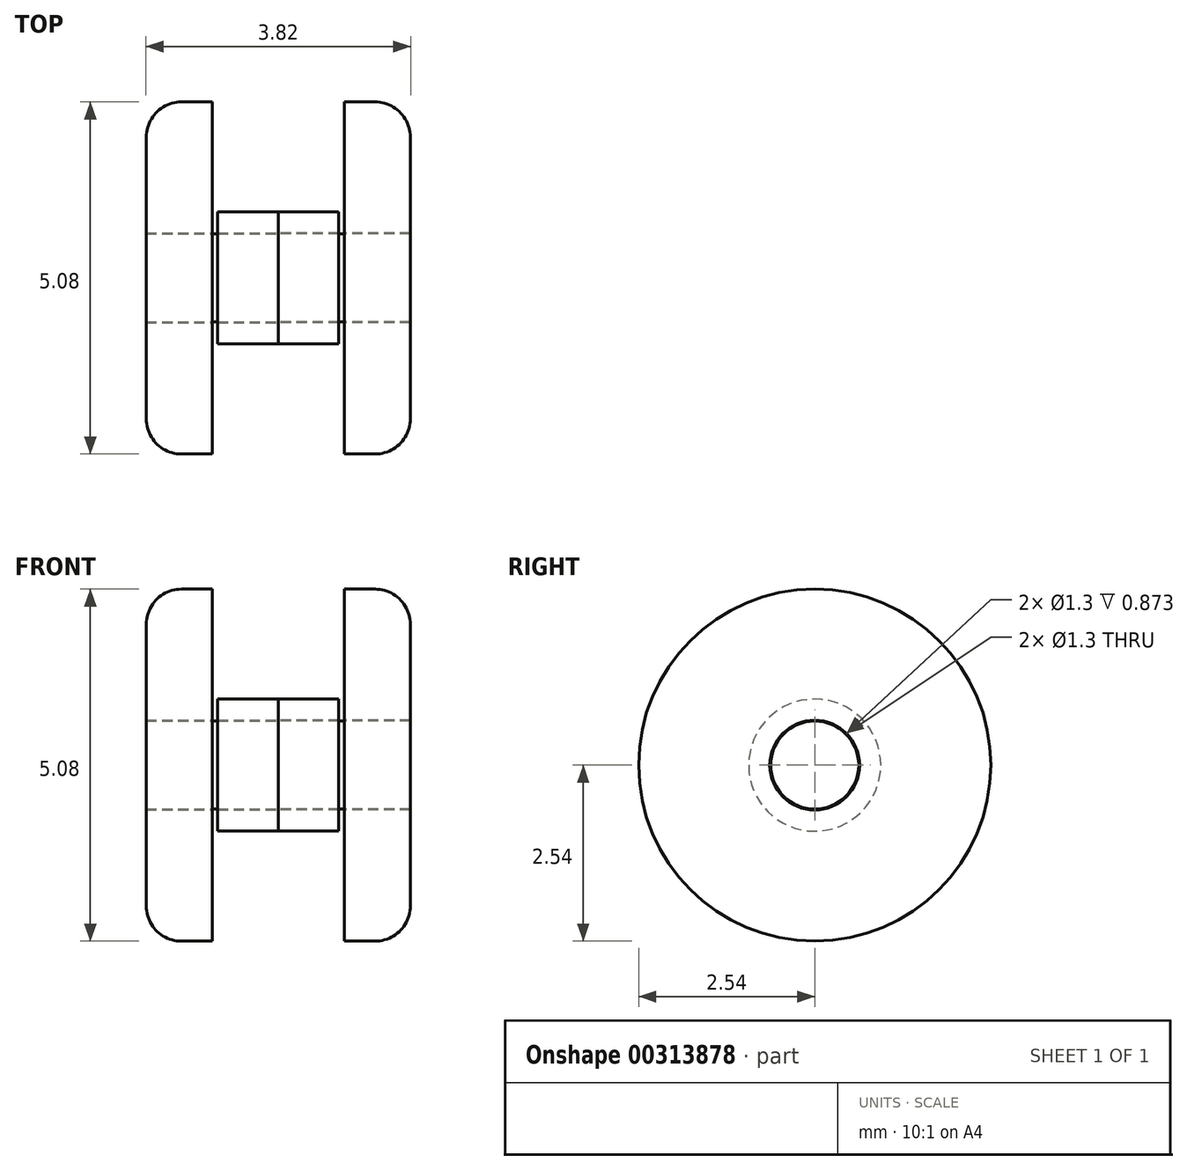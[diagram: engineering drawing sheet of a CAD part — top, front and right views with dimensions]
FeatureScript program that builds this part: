
annotation { "Feature Type Name" : "Feature", "Feature Type Description" : "" }
export const myFeature = defineFeature(function(context is Context, id is Id, definition is map)
    precondition{}
    {
        {
            var Q0;
            Q0=qCreatedBy(makeId("Right.planeOp"),FACE);
            var sketch = newSketch(context, id + "F0", { "sketchPlane" : qUnion([Q0])});
            skCircle(sketch, "E0", {"center": v(0, 0) * mm, "radius": 2.54 * mm});
            skCircle(sketch, "E1", {"center": v(0, 0) * mm, "radius": 0.64 * mm});
            skCircle(sketch, "E2", {"center": v(0, 0) * mm, "radius": 0.65 * mm});
            skCircle(sketch, "E3", {"center": v(0, 0) * mm, "radius": 0.95 * mm});
            skSolve(sketch);
        }
        {
            var Q0;
            Q0=makeQuery(id+"F0.imprint","IMPRINT",FACE,{"disambiguationData":[TD([[makeQuery(id+"F0.imprint","IMPRINT",EDGE,{"derivedFrom":sQuery(id+"F0.wireOp",EDGE,"E0")}),1.0]])]});
            extrude(context, id + "F1", {"entities" : qUnion([Q0]), "depth" : 0.95 * mm});
        }
        {
            var Q0;
            Q0=makeQuery(id+"F0.imprint","IMPRINT",FACE,{"disambiguationData":[TD([[makeQuery(id+"F0.imprint","IMPRINT",EDGE,{"derivedFrom":sQuery(id+"F0.wireOp",EDGE,"E1")}),1.0]])]});
            var Q1;
            Q1=makeQuery(id+"F0.imprint","IMPRINT",FACE,{"disambiguationData":[TD([[makeQuery(id+"F0.imprint","IMPRINT",EDGE,{"derivedFrom":sQuery(id+"F0.wireOp",EDGE,"E2")}),-1.0]])]});
            extrude(context, id + "F2", {"entities" : qUnion([Q0, Q1]), "operationType" : NewBodyOperationType.ADD, "depth" : 0.95 * mm});
        }
        {
            var Q0;
            Q0=makeQuery(id+"F1.opExtrude","SWEPT_BODY",BODY,{"disambiguationData":[OSD([sQuery(id+"F0.wireOp",EDGE,"E0"),sQuery(id+"F0.wireOp",EDGE,"E3")])]});
            var Q1;
            Q1=makeQuery(id+"F2.opExtrude","SWEPT_BODY",BODY,{"disambiguationData":[OSD([sQuery(id+"F0.wireOp",EDGE,"E1")])]});
            transform(context, id + "F3", {"entities" : qUnion([Q0, Q1]), "transformType" : TransformType.TRANSLATION_3D, "dx" : 0.95 * mm, "dy" : 0 * mm, "dz" : 0 * mm, "makeCopy" : false});
        }
        {
            var Q0;
            Q0=makeQuery(id+"F0.imprint","IMPRINT",FACE,{"disambiguationData":[TD([[makeQuery(id+"F0.imprint","IMPRINT",EDGE,{"derivedFrom":sQuery(id+"F0.wireOp",EDGE,"E1")}),1.0]])]});
            extrude(context, id + "F4", {"entities" : qUnion([Q0]), "operationType" : NewBodyOperationType.ADD, "depth" : 1.9 * mm});
        }
        {
            var Q0;
            Q0=makeQuery(id+"F0.imprint","IMPRINT",FACE,{"disambiguationData":[TD([[makeQuery(id+"F0.imprint","IMPRINT",EDGE,{"derivedFrom":sQuery(id+"F0.wireOp",EDGE,"E2")}),-1.0]])]});
            extrude(context, id + "F5", {"entities" : qUnion([Q0]), "depth" : 0.87 * mm});
        }
        {
            var Q0;
            Q0=makeQuery(id+"F1.opExtrude","SWEPT_BODY",BODY,{"disambiguationData":[OSD([sQuery(id+"F0.wireOp",EDGE,"E0"),sQuery(id+"F0.wireOp",EDGE,"E3")])]});
            var Q1;
            Q1=makeQuery(id+"F2.opExtrude","SWEPT_BODY",BODY,{"disambiguationData":[OSD([sQuery(id+"F0.wireOp",EDGE,"E1")])]});
            var Q2;
            Q2=makeQuery(id+"F5.opExtrude","SWEPT_BODY",BODY,{"disambiguationData":[OSD([sQuery(id+"F0.wireOp",EDGE,"E2"),sQuery(id+"F0.wireOp",EDGE,"E3")])]});
            var Q3;
            Q3=qCreatedBy(makeId("Right.planeOp"),FACE);
            mirror(context, id + "F6", {"entities" : qUnion([Q0, Q1, Q2]), "mirrorPlane" : qUnion([Q3])});
        }
        {
            var Q0;
            Q0=makeQuery(id+"F1.opExtrude","CAP_EDGE",EDGE,{"disambiguationData":[OSD([sQuery(id+"F0.wireOp",EDGE,"E0")])],"isStart":false});
            var Q1;
            Q1=makeQuery(id+"F6.opPattern","COPY",EDGE,{"derivedFrom":makeQuery(id+"F1.opExtrude","CAP_EDGE",EDGE,{"disambiguationData":[OSD([sQuery(id+"F0.wireOp",EDGE,"E0")])],"isStart":false}),"instanceName":"1"});
            fillet(context, id + "F7", {"entities" : qUnion([Q0, Q1]), "radius" : 0.5 * mm, "tangentPropagation" : true, "allowEdgeOverflow" : false});
        }
    });
